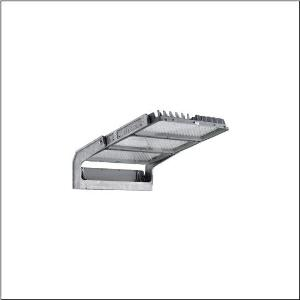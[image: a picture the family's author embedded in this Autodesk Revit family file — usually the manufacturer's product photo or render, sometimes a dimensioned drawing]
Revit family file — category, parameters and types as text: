
# Revit family: floodlight_fl_11_maxi_pro___rs08_5xa779128l01gb_a40c
name_source: partatom
category: Lighting Fixtures
units: mm (PartAtom-declared; Revit-internal decimal feet)

## family parameters
Cut with Voids When Loaded = No
Host = Face
Light Source = No
Part Type = Normal
Room Calculation Point = No
Round Connector Dimension = Use Diameter
Shared = No

## types (1)
- --- (1 x LED, 148170 lm, 1285.1 W, 5700K)
    Apparent Load = 1285 VA
    CIE Flux Codes = 70 87 98 100 100
    Color Rendering = 80
    Color Temperature = 5700K
    Default Elevation = 1800 mm
    Description = Floodlight FL 11  maxi  pro floodlight; light control with lens of PMMA; cover panel of toughened safety glass, transparent; light distribution: RS08, rotationally symmetric direct distribution, LED; colour temperature: 5700K, rated luminous flux: 148.170lm, colour rendering: CRI > 80, light colour: 857; luminous efficacy: 115lm/W; brightness control: DALI 2; with terminal, 5-pole, max. 2.5mm², mains connection: 220..240V/380..400V AC, 50/60Hz, surge voltage resistance: line to ground: 10kV, LED service life up to 100,000h L90. Typical operating time: 1000h per year., ECG replaceable separately, LED unit replaceable without ESD environment, dustproof LED module, dimming range 10..100%; 1285W floodlight with 3x LED unit of diecast aluminium, coated grey; length: 1.003mm / width: 651mm / height: 338mm; mounting bracket, of diecast aluminium, uncoated, natural, equipment: Power, protection rating (complete): IP66; insulation class (complete): insulation class I (protective earthing); certification: CE, ENEC, VDE; ball protection: ball impact resistant, only for outdoor installations in the designated locations, permissible operating ambient temperature: -45..+55°C, permissible storage temperature: -40..+85°Cpackaging unit: 1 piece

Light Distribution: RS08
    Height = 320 mm
    Lamp = 1 x LED
    Lamp Light Flux = 148170 lm
    Lamp Power = 1285.1 W
    Lamp count = 1
    Length = 1002 mm
    Luminous efficacy = 115 lm/W
    Manufacturer = Siteco
    ModVariant = No
    Model = 5XA779128L01GB
    Mounting Place = Ceiling
    Mounting Type = Surface mounted
    Number of Poles = 1
    OnlyDefault = Yes
    Power Factor = 1
    Product Name = Floodlight FL 11 maxi pro | RS08
    Product group = floodlight | ceiling mounted
    ProductGroupID = 303
    Protection Class = Protection class I
    Protection Degree = IP 66
    RLX_Detail_Level = 1
    RLX_Emergency_Light_Flux = 0 lm
    RLX_Emergency_Type = 0
    RLX_Emergency_Type_DB = No
    RlxData = <blob elided: 40269 chars, md5=c49f4bad>
    Socket = socket
    Standby Power = 0 W
    System Light Flux = 148170 lm
    System Power = 1285 W
    Type Comments = factory setting: luminous flux: 100 % | dim-lin: 254 | 875 mA
    Type Image = l_1356210.jpg
    URL = http://relux.com
    VarID = @adj_040187
    Voltage = 0 V
    Weight = 0.00 kg
    Width = 655 mm

## geometry (parser evidence)
native form markers: Blend x4, Sweep x12
no freeform markers — native parametric forms only
